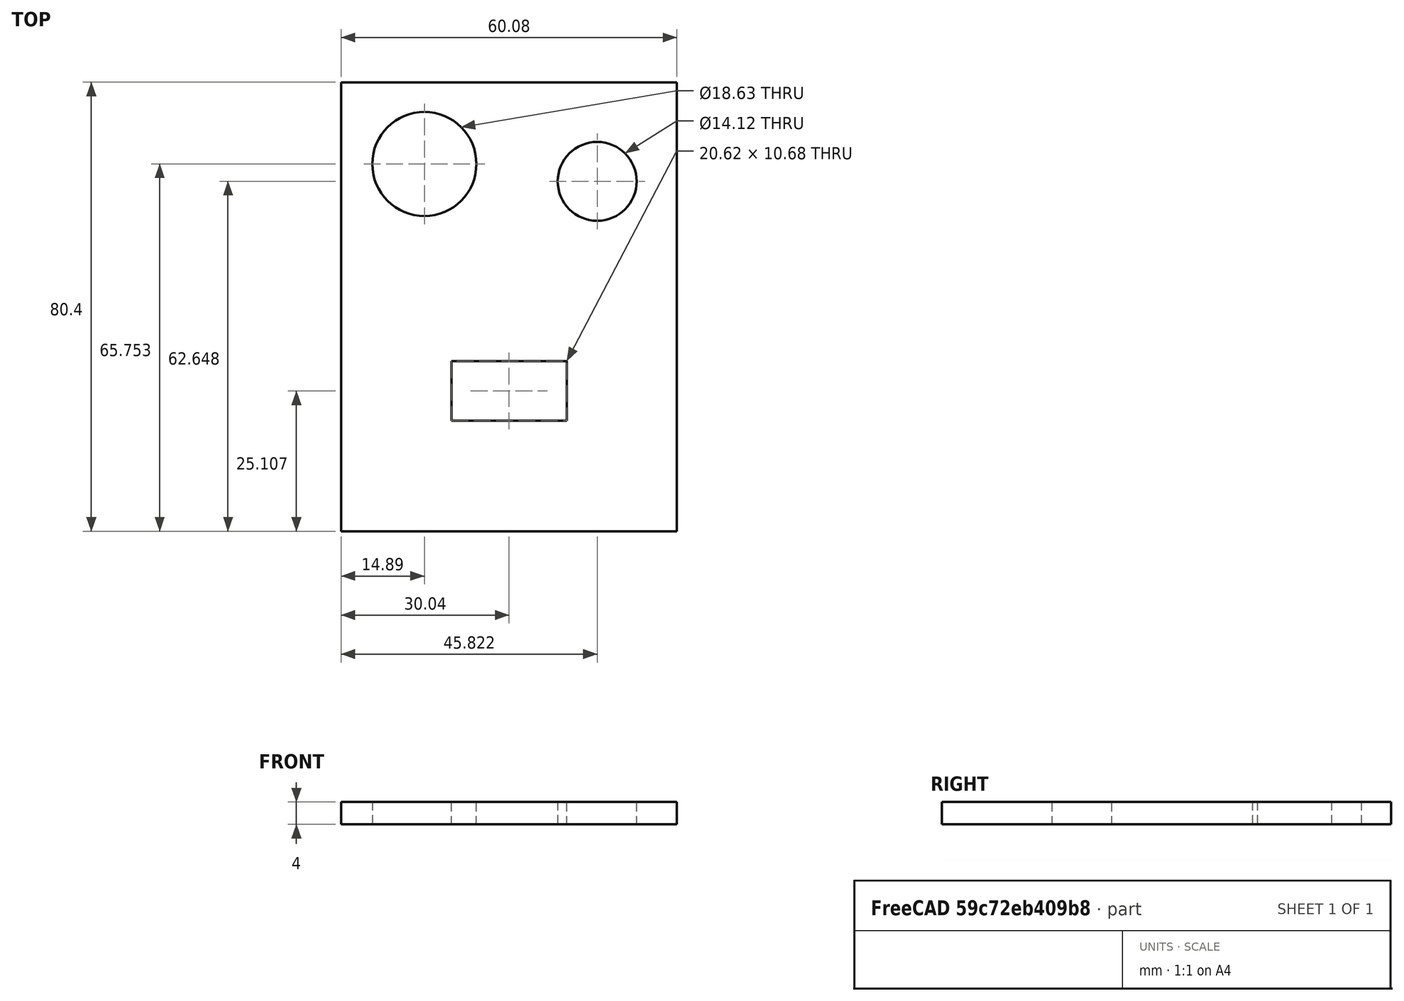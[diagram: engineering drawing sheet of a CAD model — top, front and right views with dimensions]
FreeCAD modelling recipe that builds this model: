
FCSTD DOCUMENT  (FreeCAD 1.0R38806 (Git))
Label: robot
License: All rights reserved
LicenseURL: https://en.wikipedia.org/wiki/All_rights_reserved
objects: Sketcher::SketchObject×1, Part::Extrusion×1
note: 3 computed .brp shape members not serialized (recipe doc carries the construction recipe); baked Part::Feature solids carry a one-line shape summary decoded from their .brp

FEATURE [Sketcher::SketchObject] Sketch
  ArcFitTolerance = 1e-06
  FullyConstrained = false
  MakeInternals = false
  sketch-geometry (12):
    g0: LineSegment StartX=10.3106 StartY=-20.4346 StartZ=0 EndX=10.3106 EndY=-9.75138 EndZ=0
    g1: LineSegment StartX=10.3106 StartY=-9.75138 StartZ=0 EndX=-10.3106 EndY=-9.75138 EndZ=0
    g2: LineSegment StartX=-10.3106 StartY=-9.75138 StartZ=0 EndX=-10.3106 EndY=-20.4346 EndZ=0
    g3: LineSegment StartX=-10.3106 StartY=-20.4346 StartZ=0 EndX=10.3106 EndY=-20.4346 EndZ=0
    g4: GeomPoint [constr] X=0 Y=-15.093 Z=0
    g5: Circle CenterX=-15.1499 CenterY=25.5531 CenterZ=0 NormalX=0 NormalY=0 NormalZ=1 AngleXU=0 Radius=9.31263
    g6: Circle CenterX=15.7818 CenterY=22.4475 CenterZ=0 NormalX=0 NormalY=0 NormalZ=1 AngleXU=0 Radius=7.0622
    g7: LineSegment StartX=30.0421 StartY=-40.1961 StartZ=0 EndX=30.0421 EndY=40.1961 EndZ=0
    g8: LineSegment StartX=30.0421 StartY=40.1961 StartZ=0 EndX=-30.0421 EndY=40.1961 EndZ=0
    g9: LineSegment StartX=-30.0421 StartY=40.1961 StartZ=0 EndX=-30.0421 EndY=-40.1961 EndZ=0
    g10: LineSegment StartX=-30.0421 StartY=-40.1961 StartZ=0 EndX=30.0421 EndY=-40.1961 EndZ=0
    g11: GeomPoint [constr] X=0 Y=0 Z=0
  constraints (20):
    c: Coincident(g0,g1)
    c: Coincident(g1,g2)
    c: Coincident(g2,g3)
    c: Coincident(g3,g0)
    c: Vertical(g0)
    c: Vertical(g2)
    c: Horizontal(g1)
    c: Horizontal(g3)
    c: Symmetric(g2,g0,g4)
    c: PointOnObject(g4,g-2)
    c: Coincident(g7,g8)
    c: Coincident(g8,g9)
    c: Coincident(g9,g10)
    c: Coincident(g10,g7)
    c: Vertical(g7)
    c: Vertical(g9)
    c: Horizontal(g8)
    c: Horizontal(g10)
    c: Symmetric(g9,g7,g11)
    c: Coincident(g11,g-1)
FEATURE [Part::Extrusion] Extrude
  Base = -> Sketch
  Dir = (0,0,1)
  DirMode = 0
  FaceMakerClass = Part::FaceMakerBullseye
  FaceMakerMode = 3
  LengthFwd = 4
  LengthRev = 0
  Solid = true
  Symmetric = false
